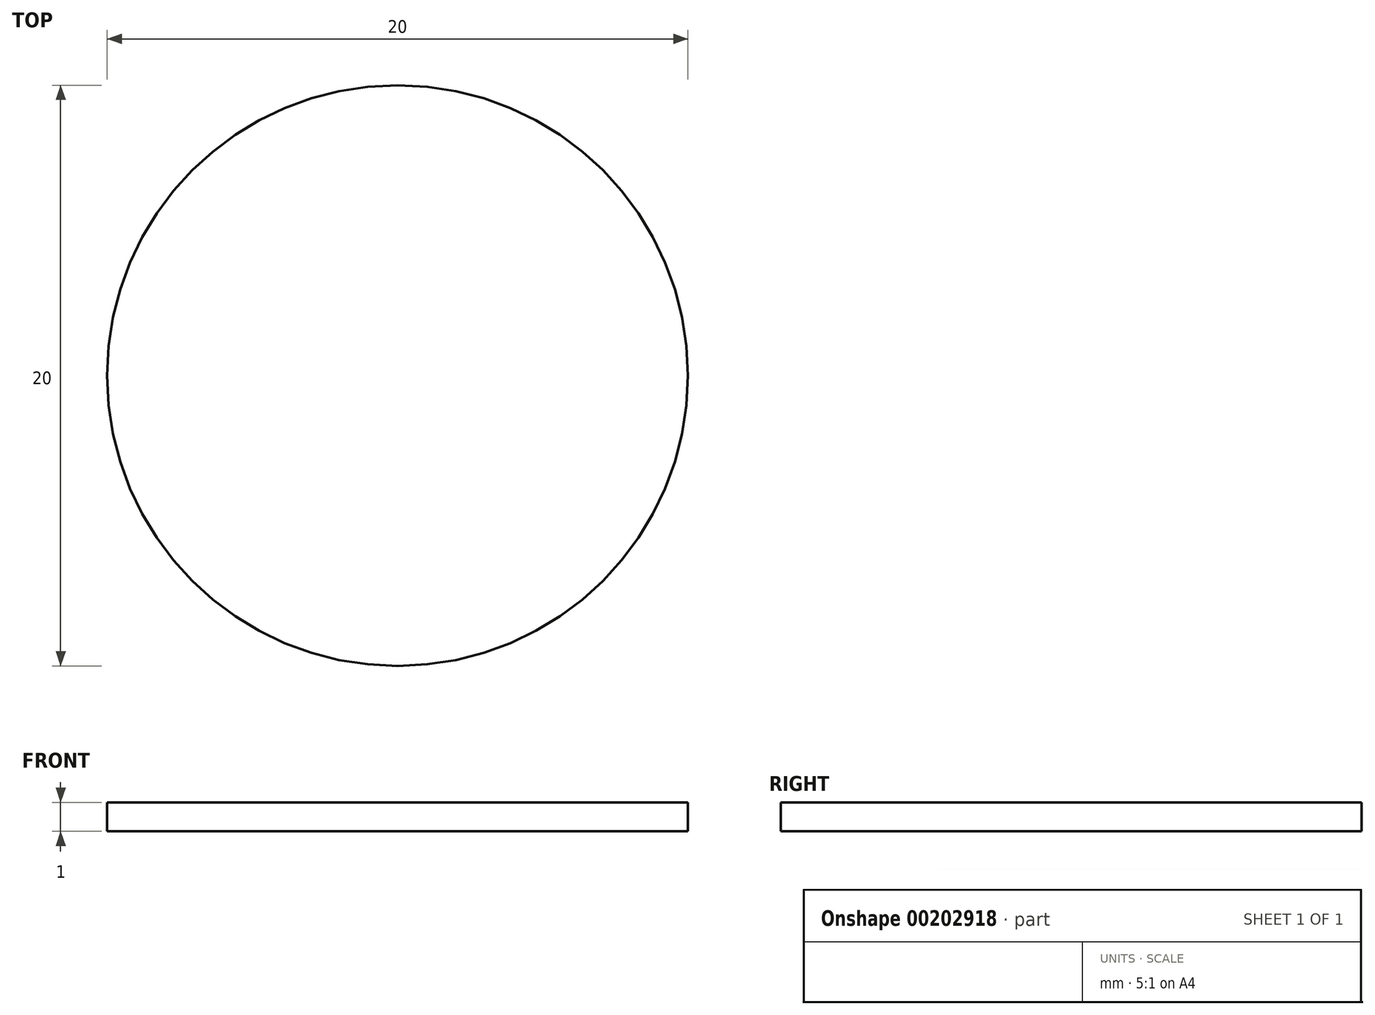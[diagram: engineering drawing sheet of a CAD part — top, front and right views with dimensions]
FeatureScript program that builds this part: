
annotation { "Feature Type Name" : "Feature", "Feature Type Description" : "" }
export const myFeature = defineFeature(function(context is Context, id is Id, definition is map)
    precondition{}
    {
        {
            var Q0;
            Q0=qCreatedBy(makeId("Top.planeOp"),FACE);
            var sketch = newSketch(context, id + "F0", { "sketchPlane" : qUnion([Q0])});
            skCircle(sketch, "E0", {"center": v(0, 0) * mm, "radius": 10 * mm});
            skSolve(sketch);
        }
        {
            var Q0;
            Q0 = qSketchRegion(id + "F0", true);
            extrude(context, id + "F1", {"entities" : qUnion([Q0]), "depth" : 1 * mm});
        }
    });
